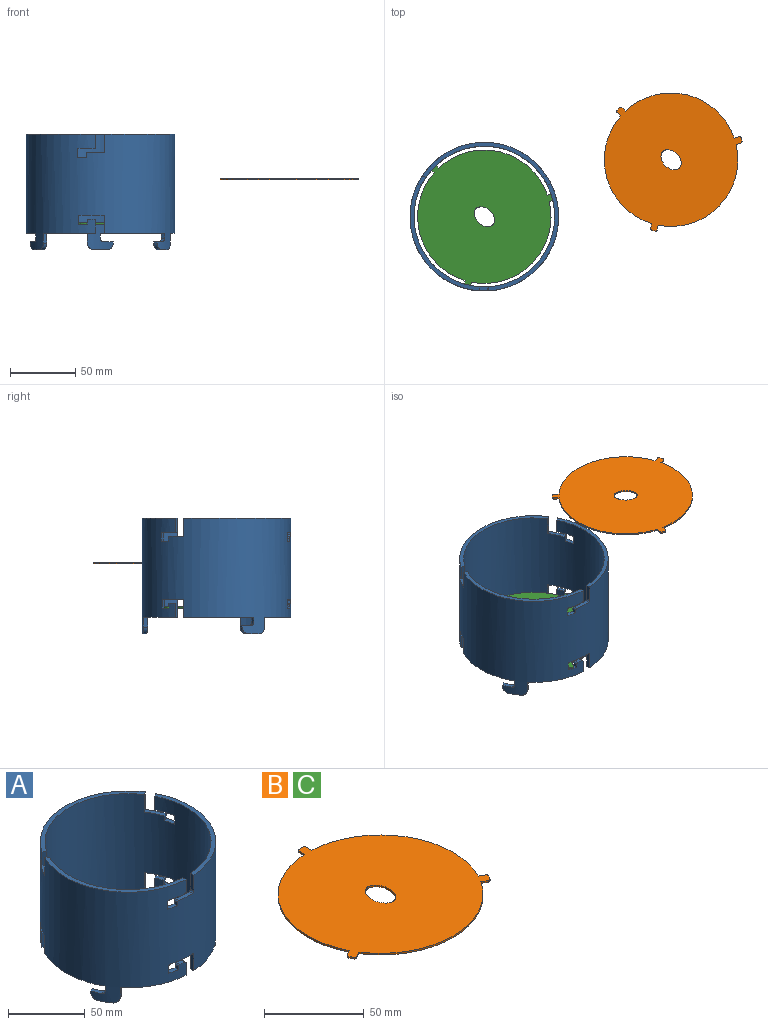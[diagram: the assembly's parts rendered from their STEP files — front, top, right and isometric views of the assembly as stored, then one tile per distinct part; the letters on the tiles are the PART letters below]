
ASSEMBLY  parts=3 mates=1
PART A: 91 faces, bbox 114.3x114.3x88.9 mm
  f0: plane 2.68x1.55mm, normal (-0.5,0.87,0), area 3.8mm2, adj f6,f7,f87,f90
  f1: plane 40.24x21.87mm, normal (0,0,-1), area 136.3mm2, adj f6,f7,f26,f82
  f2: plane 2.68x1.55mm, normal (-0.5,-0.87,0), area 3.8mm2, adj f6,f7,f78,f81
  f3: plane 45x8.62mm, normal (0,0,-1), area 136.3mm2, adj f6,f7,f62,f73
  f4: plane 3.1x1.23mm, normal (1,0,0), area 3.8mm2, adj f6,f7,f69,f72
  f5: plane 37.71x26.21mm, normal (0,0,-1), area 136.3mm2, adj f6,f7,f48,f64
  f6: cylinder r=54.1mm len=108.2mm, axis (0,0,-1), area 25419mm2, adj f0,f1,f2,f3,f4,f5,f8,f9
  f7: cylinder r=57.15mm len=114.3mm, axis (0,0,-1), area 26879.3mm2, adj f0,f1,f2,f3,f4,f5,f8,f9
  f8: plane 82.48x53.59mm, normal (0,0,1), area 333.4mm2, adj f6,f7,f20,f55
  f9: plane 40.24x21.87mm, normal (0,0,-1), area 136.3mm2, adj f6,f7,f27,f74
  f10: plane 95.24x27.08mm, normal (0,0,1), area 333.4mm2, adj f6,f7,f41,f56
  f11: plane 37.71x26.21mm, normal (0,0,-1), area 136.3mm2, adj f6,f7,f63,f65
  f12: plane 82.48x53.59mm, normal (0,0,1), area 333.4mm2, adj f6,f7,f19,f42
  f13: plane 45x8.62mm, normal (0,0,-1), area 136.3mm2, adj f6,f7,f49,f83
  f14: plane 11.68x5.42mm, normal (0,0,-1), area 36.4mm2, adj f6,f7,f32,f33
  f15: plane 5.59x3.22mm, normal (1,0,0), area 18mm2, adj f6,f7,f16,f33
  f16: plane 7.11x5.05mm, normal (0,0,1), area 22.4mm2, adj f6,f7,f15,f17
  f17: plane 3.11x2.54mm, normal (-1,0,0), area 7.9mm2, adj f6,f7,f16,f34
  f18: plane 11.68x3.87mm, normal (0,0,1), area 35.8mm2, adj f6,f7,f34,f35
  f19: plane 9.65x3.05mm, normal (1,0,0), area 29.5mm2, adj f6,f7,f12,f32
  f20: plane 12.7x3.05mm, normal (-1,0,0), area 38.8mm2, adj f6,f7,f8,f35
  f21: plane 18.03x5.39mm, normal (0,0,-1), area 55.6mm2, adj f6,f7,f28,f29
  f22: plane 5.59x3.2mm, normal (1,0,0), area 17.9mm2, adj f6,f7,f23,f29
  f23: plane 7.11x4.93mm, normal (0,0,1), area 22.4mm2, adj f6,f7,f22,f24
  f24: plane 3.1x2.54mm, normal (-1,0,0), area 7.9mm2, adj f6,f7,f23,f30
  f25: plane 3.81x3.54mm, normal (0,0,1), area 11.7mm2, adj f6,f7,f30,f31
  f26: plane 9.65x3.05mm, normal (1,0,0), area 29.5mm2, adj f1,f6,f7,f31
  f27: plane 12.7x3.05mm, normal (-1,0,0), area 38.8mm2, adj f6,f7,f9,f28
  f28: cylinder r=1.27mm len=3.12mm, axis (0,-1,0), area 6.1mm2, adj f6,f7,f21,f27
  f29: cylinder r=1.27mm len=3.58mm, axis (0,-1,0), area 6.4mm2, adj f6,f7,f21,f22
  f30: cylinder r=1.27mm len=3.31mm, axis (0,1,0), area 6.2mm2, adj f6,f7,f24,f25
  f31: cylinder r=1.27mm len=3.15mm, axis (0,1,0), area 6.1mm2, adj f6,f7,f25,f26
  f32: cylinder r=1.27mm len=3.15mm, axis (0,1,0), area 6.1mm2, adj f6,f7,f14,f19
  f33: cylinder r=1.27mm len=3.62mm, axis (0,-1,0), area 6.4mm2, adj f6,f7,f14,f15
  f34: cylinder r=1.27mm len=3.33mm, axis (0,1,0), area 6.2mm2, adj f6,f7,f17,f18
  f35: cylinder r=1.27mm len=3.12mm, axis (0,-1,0), area 6.1mm2, adj f6,f7,f18,f20
  f36: plane 12.48x12.26mm, normal (0,0,-1), area 44.3mm2, adj f6,f7,f37,f41
  f37: plane 6.86x2.79mm, normal (-0.5,-0.87,0), area 22.1mm2, adj f6,f7,f36,f38
  f38: plane 7.93x6.8mm, normal (0,0,1), area 22.4mm2, adj f6,f7,f37,f39
  f39: plane 3.81x2.69mm, normal (0.5,0.87,0), area 11.8mm2, adj f6,f7,f38,f40
  f40: plane 13.4x10.58mm, normal (0,0,1), area 43.6mm2, adj f6,f7,f39,f42
  f41: plane 10.92x2.65mm, normal (-0.5,-0.87,0), area 33.4mm2, adj f6,f7,f10,f36
  f42: plane 13.97x2.65mm, normal (0.5,0.87,0), area 42.7mm2, adj f6,f7,f12,f40
  f43: plane 18.1x15.21mm, normal (0,0,-1), area 63.6mm2, adj f6,f7,f44,f49
  f44: plane 6.86x2.77mm, normal (-0.5,-0.87,0), area 22mm2, adj f6,f7,f43,f45
  f45: plane 7.82x6.84mm, normal (0,0,1), area 22.4mm2, adj f6,f7,f44,f46
  f46: plane 3.81x2.68mm, normal (0.5,0.87,0), area 11.8mm2, adj f6,f7,f45,f47
  f47: plane 6.65x6.51mm, normal (0,0,1), area 19.5mm2, adj f6,f7,f46,f48
  f48: plane 10.92x2.65mm, normal (-0.5,-0.87,0), area 33.4mm2, adj f5,f6,f7,f47
  f49: plane 13.97x2.65mm, normal (0.5,0.87,0), area 42.7mm2, adj f6,f7,f13,f43
  f50: plane 15.29x7.4mm, normal (0,0,-1), area 44.3mm2, adj f6,f7,f51,f55
  f51: plane 6.86x2.79mm, normal (-0.5,0.87,0), area 22.1mm2, adj f6,f7,f50,f52
  f52: plane 8.68x4.66mm, normal (0,0,1), area 22.4mm2, adj f6,f7,f51,f53
  f53: plane 3.81x2.69mm, normal (0.5,-0.87,0), area 11.8mm2, adj f6,f7,f52,f54
  f54: plane 14.32x8.98mm, normal (0,0,1), area 43.6mm2, adj f6,f7,f53,f56
  f55: plane 10.92x2.65mm, normal (-0.5,0.87,0), area 33.4mm2, adj f6,f7,f8,f50
  f56: plane 13.97x2.65mm, normal (0.5,-0.87,0), area 42.7mm2, adj f6,f7,f10,f54
  f57: plane 20.66x10.78mm, normal (0,0,-1), area 63.6mm2, adj f6,f7,f58,f63
  f58: plane 6.86x2.77mm, normal (-0.5,0.87,0), area 22mm2, adj f6,f7,f57,f59
  f59: plane 8.62x4.74mm, normal (0,0,1), area 22.4mm2, adj f6,f7,f58,f60
  f60: plane 3.81x2.68mm, normal (0.5,-0.87,0), area 11.8mm2, adj f6,f7,f59,f61
  f61: plane 7.43x5.17mm, normal (0,0,1), area 19.5mm2, adj f6,f7,f60,f62
  f62: plane 10.92x2.65mm, normal (-0.5,0.87,0), area 33.4mm2, adj f3,f6,f7,f61
  f63: plane 13.97x2.65mm, normal (0.5,-0.87,0), area 42.7mm2, adj f6,f7,f11,f57
  f64: plane 7.62x3.1mm, normal (-1,0,0), area 23.6mm2, adj f5,f6,f7,f71
  f65: plane 3.1x0.05mm, normal (1,0,0), area 0.1mm2, adj f6,f7,f11,f67
  f66: plane 9.65x3.26mm, normal (0,0,-1), area 29.5mm2, adj f6,f7,f71,f72
  f67: plane 9.91x3.96mm, normal (0,0,-1), area 30.4mm2, adj f6,f7,f65,f68
  f68: plane 3.81x3.05mm, normal (1,0,0), area 11.6mm2, adj f6,f7,f67,f70
  f69: plane 7.37x3.91mm, normal (0,0,1), area 22.6mm2, adj f4,f6,f7,f70
  f70: cylinder r=2.54mm len=3.11mm, axis (0,1,0), area 12.2mm2, adj f6,f7,f68,f69
  f71: cylinder r=5.08mm len=5.08mm, axis (0,-1,0), area 24.6mm2, adj f6,f7,f64,f66
  f72: cylinder r=5.08mm len=5.08mm, axis (0,1,0), area 24.6mm2, adj f4,f6,f7,f66
  f73: plane 7.62x2.68mm, normal (0.5,0.87,0), area 23.6mm2, adj f3,f6,f7,f80
  f74: plane 2.68x1.55mm, normal (-0.5,-0.87,0), area 0.1mm2, adj f6,f7,f9,f76
  f75: plane 9.89x7.48mm, normal (0,0,-1), area 29.5mm2, adj f6,f7,f80,f81
  f76: plane 9.67x8.38mm, normal (0,0,-1), area 30.4mm2, adj f6,f7,f74,f77
  f77: plane 3.81x2.64mm, normal (-0.5,-0.87,0), area 11.6mm2, adj f6,f7,f76,f79
  f78: plane 7.5x7.07mm, normal (0,0,1), area 22.6mm2, adj f2,f6,f7,f79
  f79: cylinder r=2.54mm len=3.96mm, axis (0.87,-0.5,0), area 12.2mm2, adj f6,f7,f77,f78
  f80: cylinder r=5.08mm len=6.28mm, axis (-0.87,0.5,0), area 24.6mm2, adj f6,f7,f73,f75
  f81: cylinder r=5.08mm len=6.28mm, axis (0.87,-0.5,0), area 24.6mm2, adj f2,f6,f7,f75
  f82: plane 7.62x2.68mm, normal (0.5,-0.87,0), area 23.6mm2, adj f1,f6,f7,f89
  f83: plane 2.68x1.55mm, normal (-0.5,0.87,0), area 0.1mm2, adj f6,f7,f13,f85
  f84: plane 9.89x7.48mm, normal (0,0,-1), area 29.5mm2, adj f6,f7,f89,f90
  f85: plane 10.56x6.84mm, normal (0,0,-1), area 30.4mm2, adj f6,f7,f83,f86
  f86: plane 3.81x2.64mm, normal (-0.5,0.87,0), area 11.6mm2, adj f6,f7,f85,f88
  f87: plane 8.33x5.63mm, normal (0,0,1), area 22.6mm2, adj f0,f6,f7,f88
  f88: cylinder r=2.54mm len=3.96mm, axis (-0.87,-0.5,0), area 12.2mm2, adj f6,f7,f86,f87
  f89: cylinder r=5.08mm len=6.28mm, axis (0.87,0.5,0), area 24.6mm2, adj f6,f7,f82,f84
  f90: cylinder r=5.08mm len=6.28mm, axis (-0.87,-0.5,0), area 24.6mm2, adj f0,f6,f7,f84
PART B: 21 faces, bbox 102.6x107.6x1 mm
  f0: plane 3.81x1.02mm, normal (-1,0,0), area 3.9mm2, adj f1,f13,f14,f16
  f1: cylinder r=51.31mm len=74.67mm, axis (0,0,-1), area 104mm2, adj f0,f2,f13,f14
  f2: plane 3.3x1.91mm, normal (-0.5,0.87,0), area 3.9mm2, adj f1,f13,f14,f17
  f3: plane 2.2x1.27mm, normal (-0.87,-0.5,0), area 2.6mm2, adj f13,f14,f17,f18
  f4: plane 3.3x1.91mm, normal (0.5,-0.87,0), area 3.9mm2, adj f5,f13,f14,f18
  f5: cylinder r=51.31mm len=86.22mm, axis (0,0,-1), area 104mm2, adj f4,f6,f13,f14
  f6: plane 3.3x1.91mm, normal (-0.5,-0.87,0), area 3.9mm2, adj f5,f13,f14,f19
  f7: plane 2.2x1.27mm, normal (0.87,-0.5,0), area 2.6mm2, adj f13,f14,f19,f20
  f8: plane 3.3x1.91mm, normal (0.5,0.87,0), area 3.9mm2, adj f9,f13,f14,f20
  f9: cylinder r=51.31mm len=74.67mm, axis (0,0,-1), area 104mm2, adj f8,f10,f13,f14
  f10: plane 3.81x1.02mm, normal (1,0,0), area 3.9mm2, adj f9,f13,f14,f15
  f11: plane 2.54x1.02mm, normal (0,1,0), area 2.6mm2, adj f13,f14,f15,f16
  f12: extruded ~17.78x12.7mm, area 49mm2, adj f13,f14
  f13: plane 107.63x102.62mm, normal (0,0,1), area 8167.6mm2, adj f0,f1,f2,f3,f4,f5,f6,f7
  f14: plane 107.63x102.62mm, normal (0,0,-1), area 8167.6mm2, adj f0,f1,f2,f3,f4,f5,f6,f7
  f15: cylinder r=1.27mm len=1.27mm, axis (0,0,-1), area 2mm2, adj f10,f11,f13,f14
  f16: cylinder r=1.27mm len=1.27mm, axis (0,0,1), area 2mm2, adj f0,f11,f13,f14
  f17: cylinder r=1.27mm len=1.74mm, axis (0,0,-1), area 2mm2, adj f2,f3,f13,f14
  f18: cylinder r=1.27mm len=1.74mm, axis (0,0,1), area 2mm2, adj f3,f4,f13,f14
  f19: cylinder r=1.27mm len=1.74mm, axis (0,0,-1), area 2mm2, adj f6,f7,f13,f14
  f20: cylinder r=1.27mm len=1.74mm, axis (0,0,1), area 2mm2, adj f7,f8,f13,f14
PART C: same geometry as B
PLACE A t=(0.51,-4.26,-6.83)mm fixed
PLACE B rot(axis=(0,0,1),46.1deg) t=(144.14,39.52,-3.86)mm
PLACE C rot(axis=(0,0,1),46.1deg) t=(0.51,-4.26,-37.82)mm
MATE revolute C.f9 <-> A.f6  axis (0,0,-1) through (0.51,-4.26,-37.82)mm
